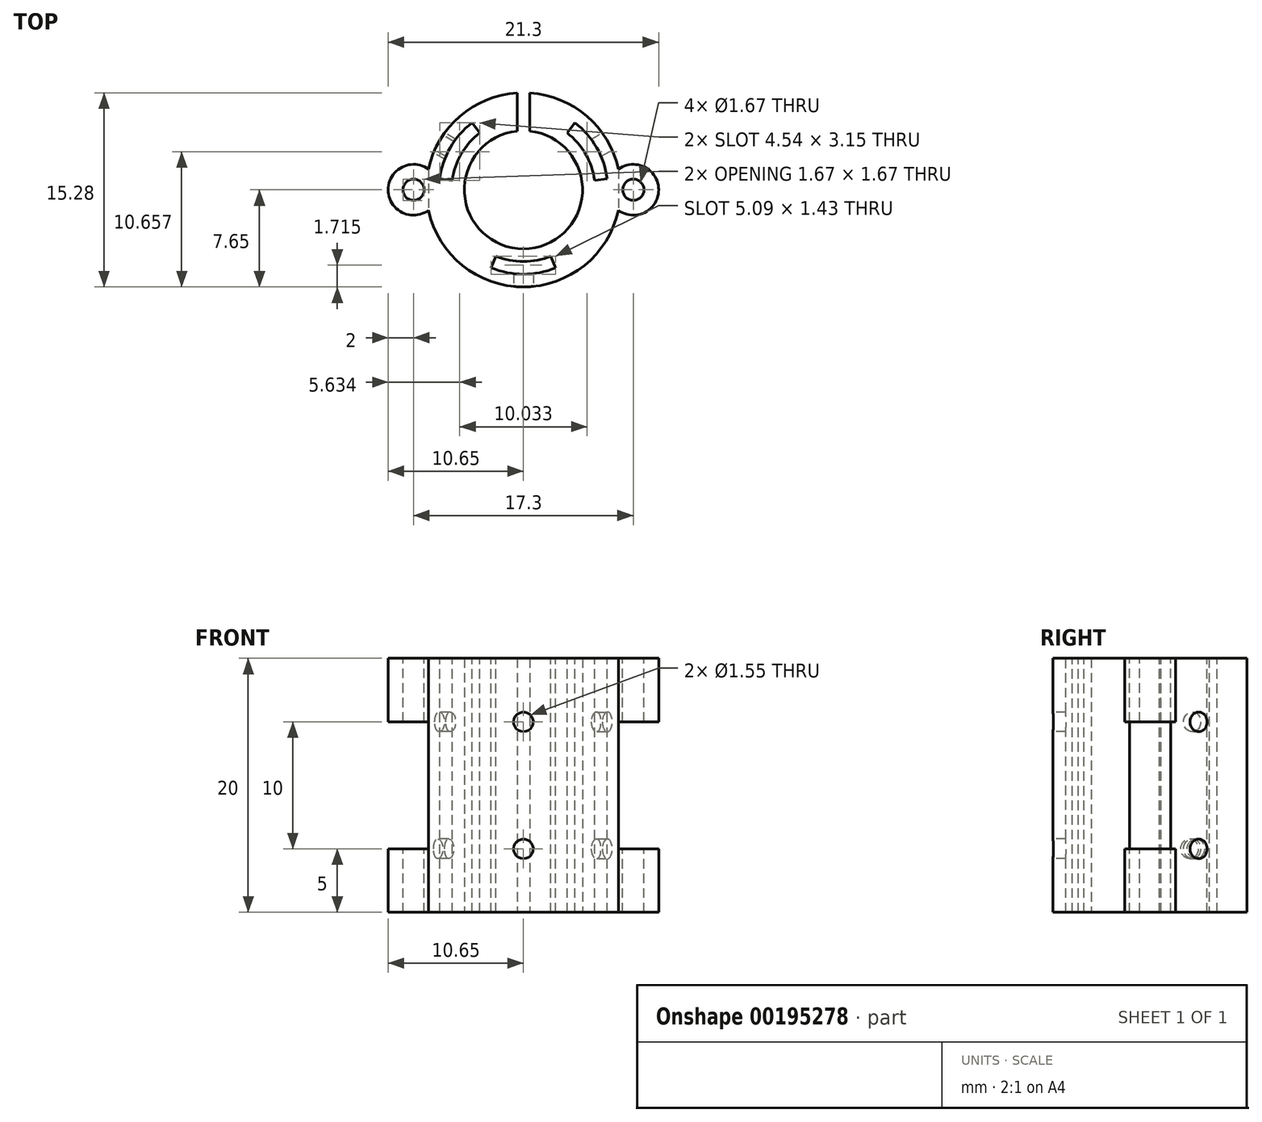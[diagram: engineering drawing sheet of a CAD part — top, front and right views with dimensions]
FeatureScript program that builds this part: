
annotation { "Feature Type Name" : "Feature", "Feature Type Description" : "" }
export const myFeature = defineFeature(function(context is Context, id is Id, definition is map)
    precondition{}
    {
        {
            var Q0;
            Q0=qCreatedBy(makeId("Top.planeOp"),FACE);
            var sketch = newSketch(context, id + "F0", { "sketchPlane" : qUnion([Q0])});
            skCircle(sketch, "E0", {"center": v(0, 0) * mm, "radius": 4.65 * mm});
            skCircle(sketch, "E1.0", {"center": v(0, 0) * mm, "radius": 7.65 * mm});
            skSolve(sketch);
        }
        {
            var Q0;
            Q0=makeQuery(id+"F0.imprint","IMPRINT",FACE,{"disambiguationData":[TD([[makeQuery(id+"F0.imprint","IMPRINT",EDGE,{"derivedFrom":sQuery(id+"F0.wireOp",EDGE,"E0")}),-1.0]])]});
            extrude(context, id + "F1", {"entities" : qUnion([Q0]), "depth" : 20 * mm});
        }
        {
            var Q0;
            Q0=makeQuery(id+"F1.opExtrude","CAP_FACE",FACE,{"disambiguationData":[OSD([sQuery(id+"F0.wireOp",EDGE,"E0"),sQuery(id+"F0.wireOp",EDGE,"E1.0")])],"isStart":false});
            var sketch = newSketch(context, id + "F2", { "sketchPlane" : qUnion([Q0])});
            skLineSegment(sketch, "E2", {"start": v(-7.65, 0) * mm, "end": v(7.65, 0) * mm, "construction": true});
            skLineSegment(sketch, "E3", {"start": v(-6.63, 3.83) * mm, "end": v(0, 0) * mm, "construction": true});
            skLineSegment(sketch, "E4", {"start": v(0, 0) * mm, "end": v(6.63, 3.83) * mm, "construction": true});
            skPoint(sketch, "E5.center", {"position": v(4.85, -1.65) * mm});
            skPoint(sketch, "E6.center", {"position": v(0, 0) * mm});
            skArc(sketch, "E7.0", {"start": v(-4.05, 5.28) * mm, "mid": v(-5.76, 3.32) * mm, "end": v(-6.6, 0.87) * mm});
            skArc(sketch, "E8.0", {"start": v(-3.44, 4.48) * mm, "mid": v(-4.9, 2.82) * mm, "end": v(-5.6, 0.74) * mm});
            skLineSegment(sketch, "E9", {"start": v(3.44, 4.48) * mm, "end": v(4.05, 5.28) * mm});
            skLineSegment(sketch, "E10", {"start": v(5.6, 0.74) * mm, "end": v(6.6, 0.87) * mm});
            skLineSegment(sketch, "E11", {"start": v(0, 0) * mm, "end": v(0, -7.65) * mm, "construction": true});
            skLineSegment(sketch, "E12", {"start": v(-3.44, 4.48) * mm, "end": v(-4.05, 5.28) * mm});
            skLineSegment(sketch, "E13", {"start": v(-5.6, 0.74) * mm, "end": v(-6.6, 0.87) * mm});
            skLineSegment(sketch, "E14", {"start": v(-2.16, -5.22) * mm, "end": v(-2.54, -6.14) * mm});
            skLineSegment(sketch, "E15", {"start": v(2.16, -5.22) * mm, "end": v(2.54, -6.14) * mm});
            skArc(sketch, "E16.trimOffspring", {"start": v(6.6, 0.87) * mm, "mid": v(5.76, 3.33) * mm, "end": v(4.05, 5.28) * mm});
            skArc(sketch, "E17.trimOffspring", {"start": v(5.6, 0.74) * mm, "mid": v(4.9, 2.83) * mm, "end": v(3.44, 4.48) * mm});
            skArc(sketch, "E18.trimOffspring", {"start": v(-2.16, -5.22) * mm, "mid": v(0, -5.65) * mm, "end": v(2.16, -5.22) * mm});
            skArc(sketch, "E19.trimOffspring", {"start": v(-2.54, -6.14) * mm, "mid": v(0, -6.65) * mm, "end": v(2.54, -6.14) * mm});
            skSolve(sketch);
        }
        {
            var Q0;
            Q0=makeQuery(id+"F1.opExtrude","CAP_FACE",FACE,{"disambiguationData":[OSD([sQuery(id+"F0.wireOp",EDGE,"E0"),sQuery(id+"F0.wireOp",EDGE,"E1.0")])],"isStart":false});
            var sketch = newSketch(context, id + "F3", { "sketchPlane" : qUnion([Q0])});
            skLineSegment(sketch, "E20", {"start": v(0, 0) * mm, "end": v(-9.8, 5.66) * mm, "construction": true});
            skLineSegment(sketch, "E21", {"start": v(0, 0) * mm, "end": v(10.66, 6.15) * mm, "construction": true});
            skLineSegment(sketch, "E22", {"start": v(0, 0) * mm, "end": v(0, -9.1) * mm, "construction": true});
            skLineSegment(sketch, "E23", {"start": v(-7.4, 2.47) * mm, "end": v(-5.93, 5.03) * mm, "construction": true});
            skLineSegment(sketch, "E24.1.0", {"start": v(1.57, -7.65) * mm, "end": v(-1.4, -7.65) * mm, "construction": true});
            skLineSegment(sketch, "E24.2.0", {"start": v(5.84, 5.18) * mm, "end": v(7.32, 2.62) * mm, "construction": true});
            skPoint(sketch, "E24.center", {"position": v(0, 0) * mm});
            skLineSegment(sketch, "E25", {"start": v(0, 0) * mm, "end": v(10.14, 0) * mm, "construction": true});
            skSolve(sketch);
        }
        {
            var Q0;
            Q0=makeQuery(id+"F2.imprint","IMPRINT",FACE,{"disambiguationData":[TD([[makeQuery(id+"F2.imprint","IMPRINT",EDGE,{"derivedFrom":sQuery(id+"F2.wireOp",EDGE,"E7.0")}),1.0]])]});
            var Q1;
            Q1=makeQuery(id+"F2.imprint","IMPRINT",FACE,{"disambiguationData":[TD([[makeQuery(id+"F2.imprint","IMPRINT",EDGE,{"derivedFrom":sQuery(id+"F2.wireOp",EDGE,"E9")}),-1.0]])]});
            var Q2;
            Q2=makeQuery(id+"F2.imprint","IMPRINT",FACE,{"disambiguationData":[TD([[makeQuery(id+"F2.imprint","IMPRINT",EDGE,{"derivedFrom":sQuery(id+"F2.wireOp",EDGE,"E14")}),1.0]])]});
            extrude(context, id + "F4", {"entities" : qUnion([Q0, Q1, Q2]), "operationType" : NewBodyOperationType.REMOVE, "endBound" : BoundingType.THROUGH_ALL, "oppositeDirection" : true, "depth" : 25 * mm});
        }
        {
            var Q0;
            Q0=sQuery(id+"F3.wireOp",EDGE,"E23");
            cPlane(context, id + "F5", {"entities" : qUnion([Q0]), "cplaneType" : CPlaneType.LINE_ANGLE, "offset" : 1 * mm, "angle" : 90 * degree, "width" : 150 * mm, "height" : 150 * mm});
        }
        {
            var Q0;
            Q0=qCreatedBy(id+"F5.planeOp",FACE);
            var sketch = newSketch(context, id + "F6", { "sketchPlane" : qUnion([Q0])});
            skCircle(sketch, "E26", {"center": v(0, 15) * mm, "radius": 0.78 * mm});
            skCircle(sketch, "E27.0.1.0", {"center": v(-0.24, 5) * mm, "radius": 0.78 * mm});
            skLineSegment(sketch, "E27.direction1", {"start": v(0, 15) * mm, "end": v(10, 15) * mm, "construction": true});
            skLineSegment(sketch, "E27.direction2", {"start": v(0, 15) * mm, "end": v(-0.24, 5) * mm, "construction": true});
            skSolve(sketch);
        }
        {
            var Q0;
            Q0 = qSketchRegion(id + "F6", true);
            extrude(context, id + "F7", {"entities" : qUnion([Q0]), "operationType" : NewBodyOperationType.REMOVE, "endBound" : BoundingType.UP_TO_NEXT, "depth" : .375 * mm});
        }
        {
            var Q0;
            Q0=sQuery(id+"F3.wireOp",EDGE,"E24.1.0");
            cPlane(context, id + "F8", {"entities" : qUnion([Q0]), "cplaneType" : CPlaneType.LINE_ANGLE, "offset" : 1 * mm, "angle" : 0 * degree, "width" : 150 * mm, "height" : 150 * mm});
        }
        {
            var Q0;
            Q0=qCreatedBy(id+"F8.planeOp",FACE);
            var sketch = newSketch(context, id + "F9", { "sketchPlane" : qUnion([Q0])});
            skCircle(sketch, "E28", {"center": v(0, 5) * mm, "radius": 0.78 * mm});
            skCircle(sketch, "E29.0.1.0", {"center": v(0, 15) * mm, "radius": 0.78 * mm});
            skLineSegment(sketch, "E29.direction1", {"start": v(0, 5) * mm, "end": v(25, 5) * mm, "construction": true});
            skLineSegment(sketch, "E29.direction2", {"start": v(0, 5) * mm, "end": v(0, 15) * mm, "construction": true});
            skSolve(sketch);
        }
        {
            var Q0;
            Q0 = qSketchRegion(id + "F9", true);
            var Q1;
            Q1=makeQuery(id+"F4.boolean.opBoolean","COPY",FACE,{"derivedFrom":makeQuery(id+"F4.opExtrude","SWEPT_FACE",FACE,{"disambiguationData":[OSD([sQuery(id+"F2.wireOp",EDGE,"E19.trimOffspring")])]})});
            extrude(context, id + "F10", {"entities" : qUnion([Q0]), "operationType" : NewBodyOperationType.REMOVE, "endBound" : BoundingType.UP_TO_NEXT, "oppositeDirection" : true, "endBoundEntityFace" : qUnion([Q1]), "depth" : 1.5 * mm});
        }
        {
            var Q0;
            Q0=sQuery(id+"F3.wireOp",EDGE,"E24.2.0");
            cPlane(context, id + "F11", {"entities" : qUnion([Q0]), "cplaneType" : CPlaneType.LINE_ANGLE, "offset" : 1 * mm, "angle" : 90 * degree, "width" : 150 * mm, "height" : 150 * mm});
        }
        {
            var Q0;
            Q0=qCreatedBy(id+"F11.planeOp",FACE);
            var sketch = newSketch(context, id + "F12", { "sketchPlane" : qUnion([Q0])});
            skCircle(sketch, "E30", {"center": v(0, 5) * mm, "radius": 0.78 * mm});
            skCircle(sketch, "E31.0.1.0", {"center": v(0, 15) * mm, "radius": 0.78 * mm});
            skLineSegment(sketch, "E31.direction1", {"start": v(0, 5) * mm, "end": v(25, 5) * mm, "construction": true});
            skLineSegment(sketch, "E31.direction2", {"start": v(0, 5) * mm, "end": v(0, 15) * mm, "construction": true});
            skSolve(sketch);
        }
        {
            var Q0;
            Q0=makeQuery(id+"F12.imprint","IMPRINT",FACE,{"disambiguationData":[TD([[makeQuery(id+"F12.imprint","IMPRINT",EDGE,{"derivedFrom":sQuery(id+"F12.wireOp",EDGE,"E30")}),1.0]])]});
            var Q1;
            Q1=makeQuery(id+"F12.imprint","IMPRINT",FACE,{"disambiguationData":[TD([[makeQuery(id+"F12.imprint","IMPRINT",EDGE,{"derivedFrom":sQuery(id+"F12.wireOp",EDGE,"E31.0.1.0")}),1.0]])]});
            extrude(context, id + "F13", {"entities" : qUnion([Q0, Q1]), "operationType" : NewBodyOperationType.REMOVE, "endBound" : BoundingType.UP_TO_NEXT, "oppositeDirection" : true, "depth" : 25 * mm});
        }
        {
            var Q0;
            Q0=makeQuery(id+"F1.opExtrude","CAP_FACE",FACE,{"disambiguationData":[OSD([sQuery(id+"F0.wireOp",EDGE,"E0"),sQuery(id+"F0.wireOp",EDGE,"E1.0")])],"isStart":true});
            var sketch = newSketch(context, id + "F14", { "sketchPlane" : qUnion([Q0])});
            skLineSegment(sketch, "E32.0", {"start": v(0, 0) * mm, "end": v(0, 9.1) * mm, "construction": true});
            skLineSegment(sketch, "E33.bottom", {"start": v(-0.5, -4.03) * mm, "end": v(0.5, -4.03) * mm});
            skLineSegment(sketch, "E33.top", {"start": v(-0.5, -9.32) * mm, "end": v(0.5, -9.32) * mm});
            skLineSegment(sketch, "E33.left", {"start": v(-0.5, -4.03) * mm, "end": v(-0.5, -9.32) * mm});
            skLineSegment(sketch, "E33.right", {"start": v(0.5, -4.03) * mm, "end": v(0.5, -9.32) * mm});
            skSolve(sketch);
        }
        {
            var Q0;
            Q0 = qSketchRegion(id + "F14", true);
            extrude(context, id + "F15", {"entities" : qUnion([Q0]), "operationType" : NewBodyOperationType.REMOVE, "endBound" : BoundingType.UP_TO_NEXT, "oppositeDirection" : true, "depth" : 25 * mm});
        }
        {
            var Q0;
            Q0=makeQuery(id+"F3.imprint","IMPRINT",FACE,{"disambiguationData":[TD([[makeQuery(id+"F3.imprint","IMPRINT",EDGE,{"derivedFrom":makeQuery(id+"F1.opExtrude","CAP_EDGE",EDGE,{"disambiguationData":[OSD([sQuery(id+"F0.wireOp",EDGE,"E0")])],"isStart":false})}),-1.0]])]});
            var sketch = newSketch(context, id + "F16", { "sketchPlane" : qUnion([Q0])});
            skPoint(sketch, "E34.orphan", {"position": v(0.5, 7.63) * mm});
            skPoint(sketch, "E35.orphan", {"position": v(-0.5, 7.63) * mm});
            skPoint(sketch, "E36.center", {"position": v(0, 0) * mm});
            skCircle(sketch, "E37", {"center": v(8.65, 0) * mm, "radius": 2 * mm});
            skCircle(sketch, "E38", {"center": v(8.65, 0) * mm, "radius": 0.84 * mm});
            skCircle(sketch, "E39.1.0", {"center": v(-8.65, 0) * mm, "radius": 0.84 * mm});
            skCircle(sketch, "E39.1.1", {"center": v(-8.65, 0) * mm, "radius": 2 * mm});
            skSolve(sketch);
        }
        {
            var Q0;
            Q0=makeQuery(id+"F16.imprint","IMPRINT",FACE,{"disambiguationData":[TD([[makeQuery(id+"F16.imprint","IMPRINT",EDGE,{"derivedFrom":sQuery(id+"F16.wireOp",EDGE,"E39.1.0")}),-1.0]])]});
            var Q1;
            Q1=makeQuery(id+"F16.imprint","IMPRINT",FACE,{"disambiguationData":[TD([[makeQuery(id+"F16.imprint","IMPRINT",EDGE,{"derivedFrom":sQuery(id+"F16.wireOp",EDGE,"E38")}),-1.0]])]});
            var Q2;
            Q2=makeQuery(id+"F1.opExtrude","CAP_FACE",FACE,{"disambiguationData":[OSD([sQuery(id+"F0.wireOp",EDGE,"E0"),sQuery(id+"F0.wireOp",EDGE,"E1.0")])],"isStart":true});
            extrude(context, id + "F17", {"entities" : qUnion([Q0, Q1]), "operationType" : NewBodyOperationType.ADD, "endBound" : BoundingType.UP_TO_SURFACE, "oppositeDirection" : true, "endBoundEntityFace" : qUnion([Q2]), "depth" : 25 * mm});
        }
        {
            var Q0;
            Q0=qCreatedBy(id+"F8.planeOp",FACE);
            var sketch = newSketch(context, id + "F18", { "sketchPlane" : qUnion([Q0])});
            skLineSegment(sketch, "E40.bottom", {"start": v(-10.65, 15) * mm, "end": v(-7.48, 15) * mm});
            skLineSegment(sketch, "E40.top", {"start": v(-10.65, 5) * mm, "end": v(-7.48, 5) * mm});
            skLineSegment(sketch, "E41", {"start": v(-10.65, 5) * mm, "end": v(-10.65, 15) * mm});
            skLineSegment(sketch, "E42.0", {"start": v(-7.48, 5) * mm, "end": v(-7.48, 15) * mm});
            skPoint(sketch, "E43.orphan", {"position": v(-7.48, 20) * mm});
            skPoint(sketch, "E44.orphan", {"position": v(-7.48, 0) * mm});
            skLineSegment(sketch, "E45", {"start": v(10.65, 15) * mm, "end": v(10.65, 5) * mm});
            skLineSegment(sketch, "E46.0", {"start": v(7.48, 5) * mm, "end": v(7.48, 15) * mm});
            skLineSegment(sketch, "E47", {"start": v(7.48, 15) * mm, "end": v(10.65, 15) * mm});
            skLineSegment(sketch, "E48", {"start": v(7.48, 5) * mm, "end": v(10.65, 5) * mm});
            skPoint(sketch, "E49.orphan", {"position": v(7.48, 20) * mm});
            skPoint(sketch, "E50.orphan", {"position": v(7.48, 0) * mm});
            skSolve(sketch);
        }
        {
            var Q0;
            Q0 = qSketchRegion(id + "F18", true);
            extrude(context, id + "F19", {"entities" : qUnion([Q0]), "operationType" : NewBodyOperationType.REMOVE, "endBound" : BoundingType.THROUGH_ALL, "oppositeDirection" : true, "depth" : 25 * mm});
        }
    });
